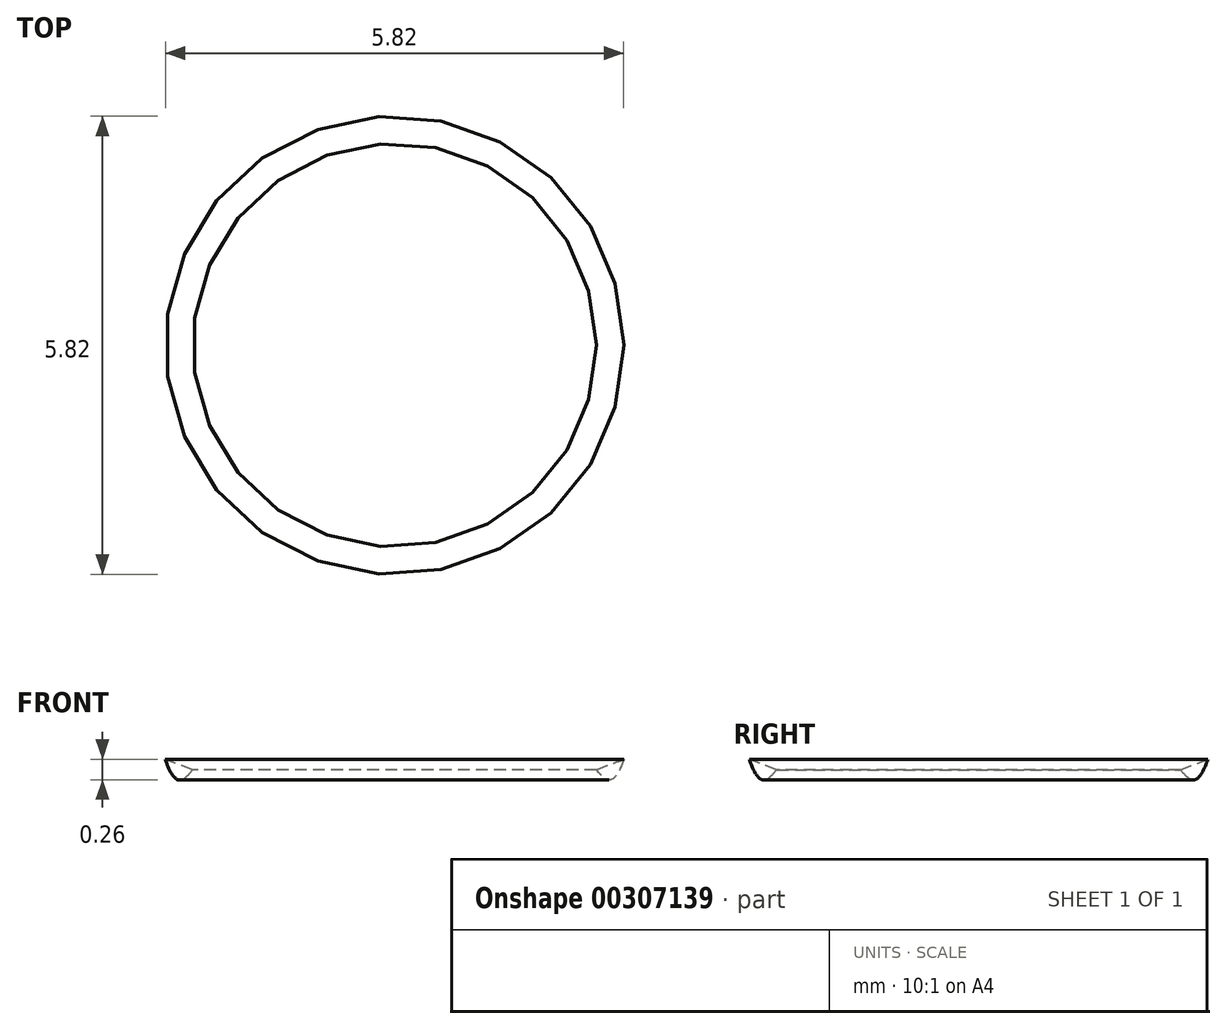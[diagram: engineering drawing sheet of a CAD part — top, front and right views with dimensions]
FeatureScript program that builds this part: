
annotation { "Feature Type Name" : "Feature", "Feature Type Description" : "" }
export const myFeature = defineFeature(function(context is Context, id is Id, definition is map)
    precondition{}
    {
        {
            var Q0;
            Q0=qCreatedBy(makeId("Front.planeOp"),FACE);
            var sketch = newSketch(context, id + "F0", { "sketchPlane" : qUnion([Q0])});
            skLineSegment(sketch, "E0", {"start": v(-9.57, 12.19) * mm, "end": v(-9.57, 12.19) * mm});
            skFitSpline(sketch, "E1", {"points": [v(-9.57, 12.19) * mm, v(-12.21, 12.19) * mm, v(-12.1, 8.56) * mm, v(-11.88, 8.67) * mm], "startDerivative": vector(-8.13, 2.85) * mm, "endDerivative": vector(1.75, 2.12) * mm});
            skFitSpline(sketch, "E2", {"points": [v(-11.88, 8.67) * mm, v(-22.55, 10.54) * mm, v(-29.92, 1.3) * mm, v(-26.07, -14.86) * mm, v(-9.57, -14.2) * mm], "startDerivative": vector(-50.25, 18.87) * mm, "endDerivative": vector(69.58, 19.44) * mm});
            skLineSegment(sketch, "E3", {"start": v(-9.57, -12.98) * mm, "end": v(-9.57, -14.2) * mm});
            skArc(sketch, "E4", {"start": v(-22.62, 9.4) * mm, "mid": v(-28.62, -1.83) * mm, "end": v(-25.33, -14.13) * mm});
            skFitSpline(sketch, "E5", {"points": [v(-22.62, 9.4) * mm, v(-21.53, 10.02) * mm, v(-9.57, 6.83) * mm], "startDerivative": vector(3.15, 3.35) * mm, "endDerivative": vector(20.02, -6.76) * mm});
            skFitSpline(sketch, "E6", {"points": [v(-25.33, -14.13) * mm, v(-23.7, -14.94) * mm, v(-21.6, -15.55) * mm, v(-18.75, -15.28) * mm, v(-15.23, -14.74) * mm, v(-9.57, -12.98) * mm], "startDerivative": vector(10.32, -5.45) * mm, "endDerivative": vector(21.65, 7.59) * mm});
            skLineSegment(sketch, "E7", {"start": v(-9.57, 6.83) * mm, "end": v(-9.57, 6.83) * mm});
            skFitSpline(sketch, "E8", {"points": [v(-9.57, 6.83) * mm, v(-11.2, 8.44) * mm, v(-11.48, 10.45) * mm, v(-10.95, 11.9) * mm, v(-9.57, 11.74) * mm, v(-9.57, 12.19) * mm], "startDerivative": vector(-7.77, 5.91) * mm, "endDerivative": vector(-1.58, 5.33) * mm});
            skLineSegment(sketch, "E9", {"start": v(-9.57, 12.19) * mm, "end": v(-9.32, 12.09) * mm});
            skLineSegment(sketch, "E10", {"start": v(-9.32, 12.09) * mm, "end": v(-9.32, 11.6) * mm});
            skLineSegment(sketch, "E11", {"start": v(-9.32, 11.6) * mm, "end": v(-9.72, 11.74) * mm});
            skSolve(sketch);
        }
        {
            var Q0;
            {var subQ4=sQuery(id+"F0.wireOp",EDGE,"E0");Q0=makeQuery(id+"F0.imprint","IMPRINT",FACE,{"disambiguationData":[TD([[makeQuery(id+"F0.imprint","IMPRINT",EDGE,{"derivedFrom":subQ4}),-1.0]])]});}
            var Q1;
            Q1=makeQuery(id+"F0.imprint","IMPRINT",FACE,{"disambiguationData":[TD([[makeQuery(id+"F0.imprint","IMPRINT",EDGE,{"derivedFrom":sQuery(id+"F0.wireOp",EDGE,"E2")}),1.0]])]});
            var Q2;
            Q2 = qConstructionFilter(qBodyType(qCreatedBy(id + "F0" ,EDGE), BodyType.WIRE), ConstructionObject.NO);
            var Q3;
            Q3=sQuery(id+"F0.wireOp",EDGE,"E10");
            revolve(context, id + "F1", {"entities" : qUnion([Q0, Q1]), "surfaceEntities" : qUnion([Q2]), "axis" : qUnion([Q3]), "revolveType" : RevolveType.FULL});
        }
        {
            var Q0;
            Q0=qCreatedBy(makeId("Front.planeOp"),FACE);
            var sketch = newSketch(context, id + "F2", { "sketchPlane" : qUnion([Q0])});
            skLineSegment(sketch, "E12", {"start": v(-19.09, 6.74) * mm, "end": v(-17.65, 5.88) * mm});
            skArc(sketch, "E13", {"start": v(-19.09, 6.74) * mm, "mid": v(-18.42, 0.43) * mm, "end": v(-12.54, 2.84) * mm});
            skLineSegment(sketch, "E14", {"start": v(-7.23, 3.07) * mm, "end": v(-5.46, 3.66) * mm});
            skArc(sketch, "E15", {"start": v(-7.23, 3.07) * mm, "mid": v(-2.01, -0.54) * mm, "end": v(0, 5.48) * mm});
            skLineSegment(sketch, "E16", {"start": v(-11, -1.92) * mm, "end": v(-11, -5.88) * mm});
            skLineSegment(sketch, "E17", {"start": v(-11, -5.88) * mm, "end": v(-12.66, -6.84) * mm});
            skLineSegment(sketch, "E18", {"start": v(-12.66, -6.84) * mm, "end": v(-11, -1.92) * mm});
            skLineSegment(sketch, "E19", {"start": v(-8.74, -1.92) * mm, "end": v(-8.74, -5.88) * mm});
            skLineSegment(sketch, "E20", {"start": v(-8.74, -5.88) * mm, "end": v(-7.26, -6.84) * mm});
            skLineSegment(sketch, "E21", {"start": v(-7.26, -6.84) * mm, "end": v(-8.74, -1.92) * mm});
            skArc(sketch, "E22", {"start": v(-21.89, -7.64) * mm, "mid": v(-21.56, -7.72) * mm, "end": v(-21.24, -7.8) * mm});
            skArc(sketch, "E23", {"start": v(-21.89, -7.64) * mm, "mid": v(-9.55, -13.99) * mm, "end": v(2.74, -7.53) * mm});
            skArc(sketch, "E24", {"start": v(-17.65, 5.88) * mm, "mid": v(-17.58, 1.8) * mm, "end": v(-13.95, 3.68) * mm});
            skArc(sketch, "E25", {"start": v(-5.46, 3.66) * mm, "mid": v(-2.46, 1.36) * mm, "end": v(-1.43, 5) * mm});
            skLineSegment(sketch, "E26", {"start": v(-21.24, -7.8) * mm, "end": v(-18.8, -10.22) * mm});
            skLineSegment(sketch, "E27", {"start": v(-18.8, -10.22) * mm, "end": v(-20, -8.08) * mm});
            skLineSegment(sketch, "E28", {"start": v(-20, -8.08) * mm, "end": v(-17.76, -10.22) * mm});
            skLineSegment(sketch, "E29", {"start": v(-17.76, -10.22) * mm, "end": v(-18.61, -8.36) * mm});
            skLineSegment(sketch, "E30", {"start": v(-18.61, -8.36) * mm, "end": v(-16.52, -10.26) * mm});
            skLineSegment(sketch, "E31", {"start": v(-16.52, -10.26) * mm, "end": v(-17.26, -8.59) * mm});
            skLineSegment(sketch, "E32", {"start": v(-17.26, -8.59) * mm, "end": v(-15.45, -10.26) * mm});
            skLineSegment(sketch, "E33", {"start": v(-15.45, -10.26) * mm, "end": v(-16.2, -8.74) * mm});
            skLineSegment(sketch, "E34", {"start": v(-16.2, -8.74) * mm, "end": v(-14.05, -10.26) * mm});
            skLineSegment(sketch, "E35", {"start": v(-14.05, -10.26) * mm, "end": v(-14.93, -8.9) * mm});
            skLineSegment(sketch, "E36", {"start": v(-14.93, -8.9) * mm, "end": v(-13.1, -10.26) * mm});
            skLineSegment(sketch, "E37", {"start": v(-13.1, -10.26) * mm, "end": v(-13.6, -9.01) * mm});
            skLineSegment(sketch, "E38", {"start": v(-13.6, -9.01) * mm, "end": v(-12.18, -10.26) * mm});
            skLineSegment(sketch, "E39", {"start": v(-12.18, -10.26) * mm, "end": v(-12.75, -9.07) * mm});
            skLineSegment(sketch, "E40", {"start": v(-12.75, -9.07) * mm, "end": v(-10.62, -10.93) * mm});
            skLineSegment(sketch, "E41", {"start": v(-8.74, -10.93) * mm, "end": v(-7.1, -9.1) * mm});
            skLineSegment(sketch, "E42", {"start": v(-7.1, -9.1) * mm, "end": v(-7.5, -10.26) * mm});
            skLineSegment(sketch, "E43", {"start": v(-7.5, -10.26) * mm, "end": v(-6.42, -9.05) * mm});
            skLineSegment(sketch, "E44", {"start": v(-6.42, -9.05) * mm, "end": v(-6.8, -10.26) * mm});
            skLineSegment(sketch, "E45", {"start": v(-6.8, -10.26) * mm, "end": v(-5.23, -8.95) * mm});
            skLineSegment(sketch, "E46", {"start": v(-5.23, -8.95) * mm, "end": v(-6, -10.26) * mm});
            skLineSegment(sketch, "E47", {"start": v(-6, -10.26) * mm, "end": v(-3.94, -8.81) * mm});
            skLineSegment(sketch, "E48", {"start": v(-3.94, -8.81) * mm, "end": v(-5.23, -10.26) * mm});
            skLineSegment(sketch, "E49", {"start": v(-5.23, -10.26) * mm, "end": v(-2.57, -8.63) * mm});
            skLineSegment(sketch, "E50", {"start": v(-2.57, -8.63) * mm, "end": v(-4.26, -10.53) * mm});
            skLineSegment(sketch, "E51", {"start": v(-4.26, -10.53) * mm, "end": v(-1.37, -8.43) * mm});
            skLineSegment(sketch, "E52", {"start": v(-1.37, -8.43) * mm, "end": v(-2.56, -10.26) * mm});
            skLineSegment(sketch, "E53", {"start": v(-2.56, -10.26) * mm, "end": v(-0.34, -8.24) * mm});
            skLineSegment(sketch, "E54", {"start": v(-0.34, -8.24) * mm, "end": v(-1.4, -10.26) * mm});
            skLineSegment(sketch, "E55", {"start": v(-1.4, -10.26) * mm, "end": v(0.81, -8) * mm});
            skLineSegment(sketch, "E56", {"start": v(0.81, -8) * mm, "end": v(0, -9.86) * mm});
            skLineSegment(sketch, "E57", {"start": v(0, -9.86) * mm, "end": v(2.23, -7.66) * mm});
            skArc(sketch, "E58.trimOffspring", {"start": v(2.23, -7.66) * mm, "mid": v(2.49, -7.6) * mm, "end": v(2.74, -7.53) * mm});
            skPoint(sketch, "E59.start.orphan", {"position": v(-8.74, -9.15) * mm});
            skLineSegment(sketch, "E60", {"start": v(-10.62, -10.93) * mm, "end": v(-11.38, -9.08) * mm});
            skLineSegment(sketch, "E61", {"start": v(-8.74, -10.93) * mm, "end": v(-8.22, -9.14) * mm});
            skLineSegment(sketch, "E62", {"start": v(-8.22, -9.14) * mm, "end": v(-9.44, -10.93) * mm});
            skLineSegment(sketch, "E63", {"start": v(-9.44, -10.93) * mm, "end": v(-9.44, -9.08) * mm});
            skLineSegment(sketch, "E64", {"start": v(-11.38, -9.08) * mm, "end": v(-10.1, -10.93) * mm});
            skLineSegment(sketch, "E65", {"start": v(-10.1, -10.93) * mm, "end": v(-10.1, -9.33) * mm});
            skLineSegment(sketch, "E66", {"start": v(-9.44, -9.08) * mm, "end": v(-10.06, -9.08) * mm});
            skLineSegment(sketch, "E67", {"start": v(-10.1, -9.33) * mm, "end": v(-10.06, -9.08) * mm});
            skLineSegment(sketch, "E68", {"start": v(-13.95, 3.68) * mm, "end": v(-12.54, 2.84) * mm});
            skLineSegment(sketch, "E69", {"start": v(-1.43, 5) * mm, "end": v(0, 5.48) * mm});
            skSolve(sketch);
        }
        {
            var Q0;
            Q0 = qSketchRegion(id + "F2", true);
            extrude(context, id + "F3", {"entities" : qUnion([Q0]), "operationType" : NewBodyOperationType.REMOVE, "offsetDistance" : 25.4 * mm, "depth" : 25.4 * mm});
        }
    });
